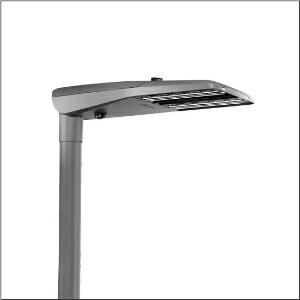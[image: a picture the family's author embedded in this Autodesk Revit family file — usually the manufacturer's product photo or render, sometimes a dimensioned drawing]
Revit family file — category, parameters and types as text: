
# Revit family: streetlight_sl_11_iq_midi___st1_2a_5xc3a61y08me_9d9d
name_source: partatom
category: Lighting Fixtures
units: mm (PartAtom-declared; Revit-internal decimal feet)

## family parameters
Cut with Voids When Loaded = No
Host = Face
Light Source = No
Part Type = Normal
Room Calculation Point = No
Round Connector Dimension = Use Diameter
Shared = No

## types (1)
- --- (1 x LED, 16240 lm, 122.7 W, 2700K)
    Apparent Load = 123 VA
    CIE Flux Codes = 32 70 96 100 100
    Color Rendering = 70
    Color Temperature = 2700K
    Default Elevation = 1800 mm
    Description = Streetlight SL 11 iQ midi, mast luminaire, primary light control with 3 zone facetted reflector, of plastic, silver coated, highly specular, primary optical cover: cover, of PMMA, transparent, light distribution: ST1.2a, light emission: direct distribution, primary light characteristic: asymmetric, installation type: post-top, side-entry, LED, High Power LED, rated luminous flux: 16.240lm, luminous efficacy: 132lm/W, light colour: 727, colour temperature: 2700K, control: pre-setting: logarithmic dimming characteristic, Street-Remote, Auto-Match, Temp-Guard, Lumen-Switch, Night-Set, Smart-Wire, Light-Fading, Desk-Remote (wireless, voltage-free reading and setting of iQ features in the workshop via application-optimized NFC function/RFID function), optimised constant luminous flux control (CLO 2.0), with cable H07RN-F 5x 1.5mm², mains connection: 230..240V, AC, 50/60Hz, connection cable pre-assembled, cable length: 12,5m, start of lifetime: 123W, end of service life: 130W, reduction: 56W, luminaire housing, of diecast aluminium, powder-coated, Siteco® metallic grey (DB 702S), please order mast flange separately, inclination adjustable without tools: 0°, 5°, 10°, 15° (post-top) | 0°, -5°, -10°, -15° (side-entry), sealing non-destructively replaceable, multi-level sealing system, length: 780mm, width: 376mm, height: 118mm, mast flange for spigot size: 42mm (side-entry): 5XC10008XM4, 60/48mm (side-entry/post-top): 5XC10108XM2, 76/60mm (side-entry/post-top): 5XC10108XM1, equipment: Power, Smart Interface below and above, protection rating (complete): IP66, insulation class (complete): insulation class II (safety insulation), certification: CE, ENEC, VDE, UKCA, impact resistance: IK09, permissible operating ambient temperature for outdoor applications: -25..+50°C, standard-compliant lighting for roads and squares, Environmental Product Declaration (EPD) tested and certified by an independent institute, packaging unit: 1 piece

Light Distribution: ST1.2a
    Height = 118 mm
    Lamp = 1 x LED
    Lamp Light Flux = 16240 lm
    Lamp Power = 122.7 W
    Lamp count = 1
    Length = 780 mm
    Luminous efficacy = 132 lm/W
    Manufacturer = Siteco
    ModVariant = No
    Model = 5XC3A61Y08ME
    Number of Poles = 1
    OnlyDefault = Yes
    Power Factor = 1
    Product Name = Streetlight SL 11 iQ midi | ST1.2a
    Product group = mast luminaire | pylon top
    ProductGroupID = 6100
    Protection Class = Protection class II
    Protection Degree = IP 66
    RLX_Detail_Level = 1
    RLX_Emergency_Light_Flux = 0 lm
    RLX_Emergency_Type = 0
    RLX_Emergency_Type_DB = No
    RlxData = <blob elided: 69841 chars, md5=88cb35dd>
    Socket = socket
    Standby Power = 0 W
    System Light Flux = 16241 lm
    System Power = 123 W
    Type Comments = factory setting: luminous flux: 100 % | dim-lin: 254 | 553 mA
    Type Image = l_1004429.jpg
    URL = http://relux.com
    VarID = @adj_102841
    Voltage = 0 V
    Weight = 0.00 kg
    Width = 376 mm

## geometry (parser evidence)
native form markers: Blend x4, Sweep x9
no freeform markers — native parametric forms only
